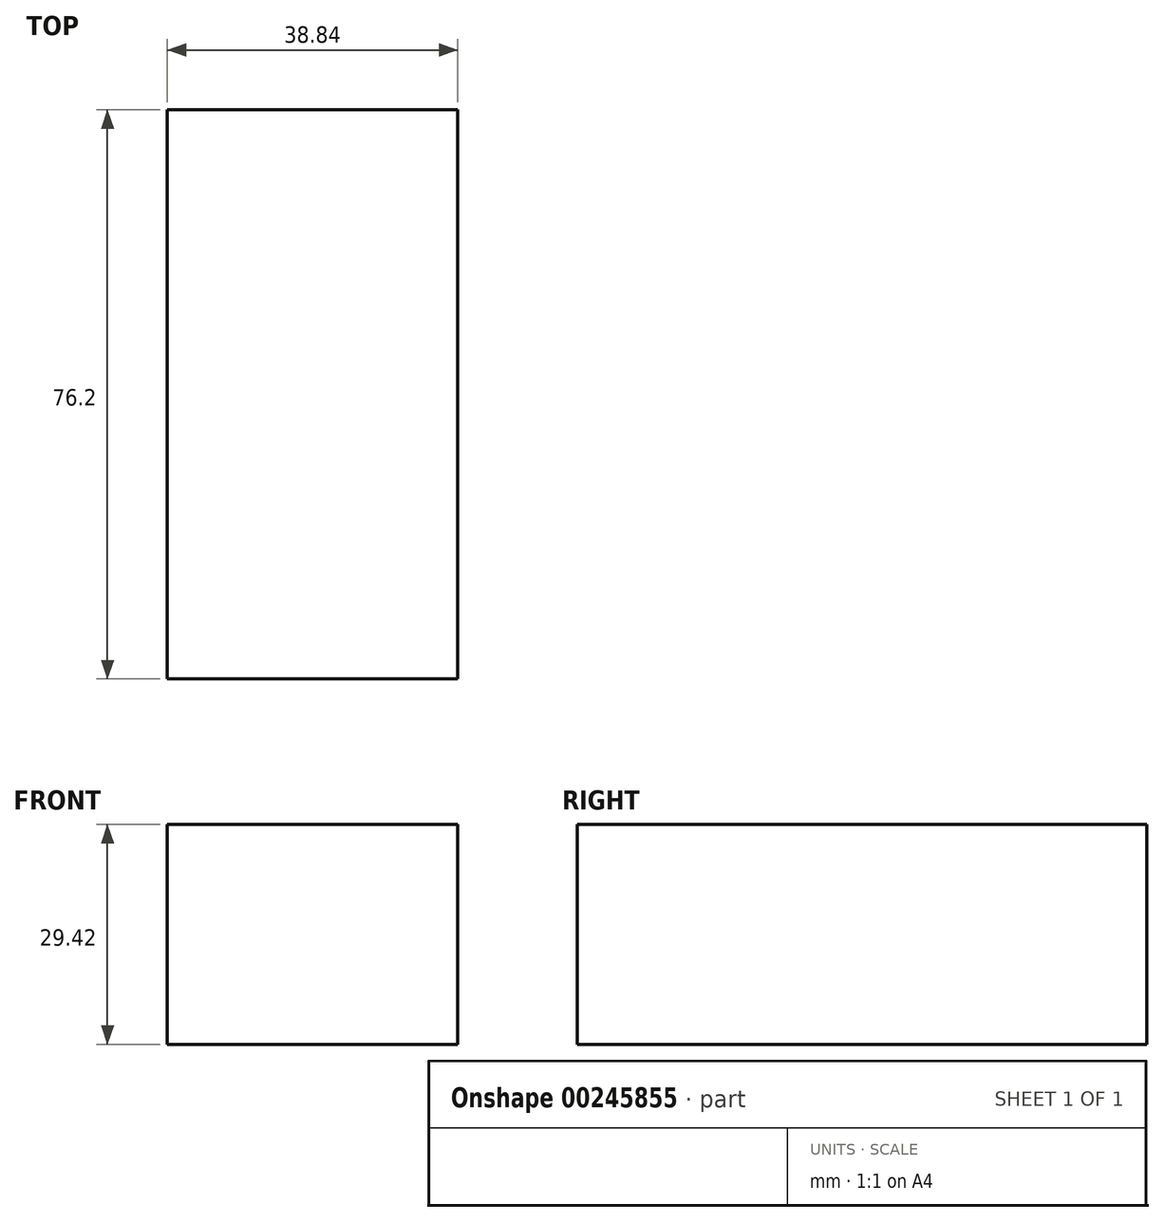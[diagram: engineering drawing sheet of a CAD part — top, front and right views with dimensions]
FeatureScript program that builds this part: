
annotation { "Feature Type Name" : "Feature", "Feature Type Description" : "" }
export const myFeature = defineFeature(function(context is Context, id is Id, definition is map)
    precondition{}
    {
        {
            var Q0;
            Q0=qCreatedBy(makeId("Front.planeOp"),FACE);
            var sketch = newSketch(context, id + "F0", { "sketchPlane" : qUnion([Q0])});
            skLineSegment(sketch, "E0", {"start": v(0, 0) * mm, "end": v(0, 38.1) * mm});
            skLineSegment(sketch, "E1", {"start": v(0, 38.1) * mm, "end": v(-27.1, 64.89) * mm});
            skLineSegment(sketch, "E2", {"start": v(-27.1, 64.89) * mm, "end": v(-63.6, 54.02) * mm});
            skLineSegment(sketch, "E3.bottom", {"start": v(19.42, -14.71) * mm, "end": v(-19.42, -14.71) * mm});
            skLineSegment(sketch, "E3.top", {"start": v(19.42, 14.71) * mm, "end": v(-19.42, 14.71) * mm});
            skLineSegment(sketch, "E3.left", {"start": v(19.42, -14.71) * mm, "end": v(19.42, 14.71) * mm});
            skLineSegment(sketch, "E3.right", {"start": v(-19.42, -14.71) * mm, "end": v(-19.42, 14.71) * mm});
            skPoint(sketch, "E3.middle", {"position": v(0, 0) * mm});
            skSolve(sketch);
        }
        {
            var Q0;
            Q0=makeQuery(id+"F0.imprint","IMPRINT",FACE,{"disambiguationData":[TD([[makeQuery(id+"F0.imprint","IMPRINT",EDGE,{"derivedFrom":sQuery(id+"F0.wireOp",EDGE,"E3.bottom")}),-1.0]])]});
            extrude(context, id + "F1", {"entities" : qUnion([Q0]), "depth" : 76.2 * mm});
        }
        {
            var Q0;
            Q0=makeQuery(id+"F1.opExtrude","CAP_FACE",FACE,{"disambiguationData":[OSD([sQuery(id+"F0.wireOp",EDGE,"E3.bottom"),sQuery(id+"F0.wireOp",EDGE,"E3.top"),sQuery(id+"F0.wireOp",EDGE,"E3.left"),sQuery(id+"F0.wireOp",EDGE,"E3.right")])],"isStart":false});
            extrude(context, id + "F2", {"entities" : qUnion([Q0]), "operationType" : NewBodyOperationType.ADD, "oppositeDirection" : true, "depth" : 12.7 * mm});
        }
    });
